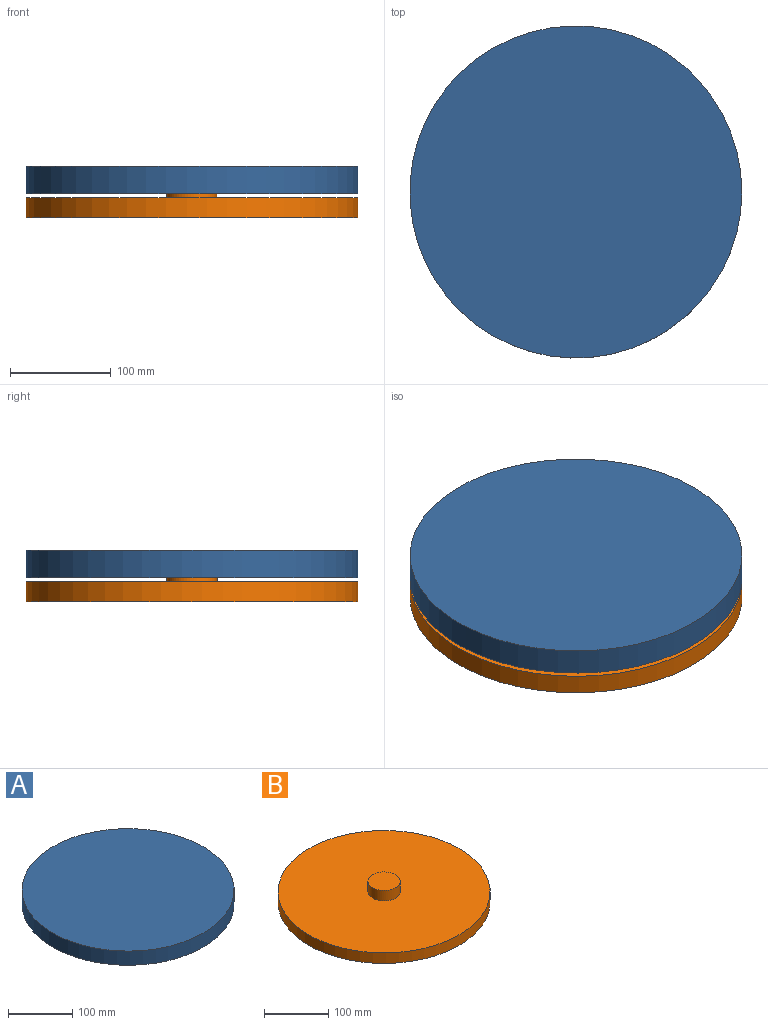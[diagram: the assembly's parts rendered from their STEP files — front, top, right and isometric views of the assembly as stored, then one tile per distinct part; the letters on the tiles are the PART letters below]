
ASSEMBLY  parts=2 mates=1
PART A: 5 faces, bbox 330x330x27 mm
  f0: cylinder r=165mm len=330mm, axis (0,0,-1), area 27991.6mm2, adj f1,f2
  f1: plane 330x330mm, normal (0,0,1), area 85529.9mm2, adj f0
  f2: plane 330x330mm, normal (0,0,-1), area 83566.4mm2, adj f0,f3
  f3: cylinder r=25mm len=50mm, axis (0,0,-1), area 2513.3mm2, adj f2,f4
  f4: plane 50x50mm, normal (0,0,-1), area 1963.5mm2, adj f3
PART B: 5 faces, bbox 330x330x40 mm
  f0: cylinder r=165mm len=330mm, axis (0,0,-1), area 20734.5mm2, adj f1,f2
  f1: plane 330x330mm, normal (0,0,1), area 83566.4mm2, adj f0,f3
  f2: plane 330x330mm, normal (0,0,-1), area 85529.9mm2, adj f0
  f3: cylinder r=25mm len=50mm, axis (0,0,-1), area 3141.6mm2, adj f1,f4
  f4: plane 50x50mm, normal (0,0,1), area 1963.5mm2, adj f3
PLACE A at identity
PLACE B t=(614.53,29.62,-24)mm
MATE revolute B.f0 <-> A.f0  axis (0,0,1) through (261.96,29.62,16)mm
